# Revit family: Golf-IP40-Plain_Door-syst-NoHosted-CH-en
name_source: partatom
category: Electrical Equipment
units: mm (PartAtom-declared; Revit-internal decimal feet)

## family parameters
Always vertical = Yes
Cut with Voids When Loaded = No
Panel Configuration = Two Columns, Circuits Across
Part Type = Panelboard
Room Calculation Point = No
Round Connector Dimension = Use Diameter
Shared = No
Work Plane-Based = Yes

## types (22) — shared parameters
Default Elevation = 1219 mm
EF000007 - Colour = EV000202 - White
EF000049 - Depth = 98 mm  [stored 0.321522 ft]
EF000116 - RAL-number = 9010
EF000118 - With mounting plate = No
EF000339 - Type of cover = EV004216 - Door
EF001062 - EMC-version = No
EF001088 - Extension possible = Yes
EF001134 - DIN-rail = Yes
EF001596 - Material housing = EV000139 - Plastic
EF004462 - Type of closure = EV000154 - Other
EF005474 - Degree of protection (IP) = EV006415 - IP40
EF006244 - Transparent cover/door = No
EF006306 - With lock = No
EF015776 - Earthing terminal block = No
EF015777 - Neutral terminal block = No
EF015941 - Signal passing door = No
HG000001 - Number of columns = 1
HG000002 - With door or cover = Yes
HG000003 - Range = Golf
HG000005 - Thickness = 3 mm  [stored 0.00984252 ft]
HG000009 - Double swing door = No
HG000010 - Asymmetric doors = No
HG000011 - Empty rows from bottom = No
Manufacturer = Hager
Type Comments = Golf
zero-valued in all types: HG000007 - Number of empty columns, HG000008 - Number of empty rows

## per-type parameters (varying)
| type | EF000003 - Mounting method | EF000008 - Width | EF000040 - Height | EF000218 - Built-in depth | EF000266 - Number of rows | EF000332 - Built-in height | EF000846 - Built-in width | EF001131 - Internal depth | EF002950 - Width in number of modular spacings | EF009212 - Cover model | HG000004 - Manufacturer reference | HG000006 - Flush mounted | Model |
| Recessed mounted IP40 W204 H225 D97.5 4 Modular spacings - VF104PS | EV000128 - Hollow wall | 204 mm | 225 mm  [stored 0.738189 ft] | 72 mm  [stored 0.23622 ft] | 1 | 189 mm  [stored 0.620079 ft] | 170 mm  [stored 0.557743 ft] | 98 mm  [stored 0.321522 ft] | 4 | EV000116 - Closed | VF104PS | Yes | VF104PS |
| Recessed mounted IP40 W275 H225 D97.5 8 Modular spacings - VF108PS | EV000128 - Hollow wall | 275 mm | 225 mm  [stored 0.738189 ft] | 72 mm  [stored 0.23622 ft] | 1 | 189 mm  [stored 0.620079 ft] | 242 mm  [stored 0.793963 ft] | 98 mm  [stored 0.321522 ft] | 8 | EV000116 - Closed | VF108PS | Yes | VF108PS |
| Recessed mounted IP40 W352 H293 D97.5 12 Modular spacings - VF112PS | EV000128 - Hollow wall | 352 mm  [stored 1.15486 ft] | 293 mm | 72 mm  [stored 0.23622 ft] | 1 | 257 mm  [stored 0.843176 ft] | 318 mm  [stored 1.04331 ft] | 98 mm  [stored 0.321522 ft] | 12 | EV000116 - Closed | VF112PS | Yes | VF112PS |
| Recessed mounted IP40 W352 H418 D97.5 12 Modular spacings - VF212PS | EV000128 - Hollow wall | 352 mm  [stored 1.15486 ft] | 418 mm  [stored 1.37139 ft] | 72 mm  [stored 0.23622 ft] | 2 | 382 mm  [stored 1.25328 ft] | 318 mm  [stored 1.04331 ft] | 98 mm  [stored 0.321522 ft] | 12 | EV000116 - Closed | VF212PS | Yes | VF212PS |
| Recessed mounted IP40 W352 H543 D97.5 12 Modular spacings - VF312PS | EV000128 - Hollow wall | 352 mm  [stored 1.15486 ft] | 543 mm  [stored 1.7815 ft] | 72 mm  [stored 0.23622 ft] | 3 | 507 mm  [stored 1.66339 ft] | 318 mm  [stored 1.04331 ft] | 98 mm  [stored 0.321522 ft] | 12 | EV000116 - Closed | VF312PS | Yes | VF312PS |
| Recessed mounted IP40 W352 H688 D97.5 12 Modular spacings - VF412PS | EV000128 - Hollow wall | 352 mm  [stored 1.15486 ft] | 688 mm  [stored 2.25722 ft] | 72 mm  [stored 0.23622 ft] | 4 | 652 mm  [stored 2.13911 ft] | 318 mm  [stored 1.04331 ft] | 98 mm  [stored 0.321522 ft] | 12 | EV000116 - Closed | VF412PS | Yes | VF412PS |
| Recessed mounted IP40 W460 H293 D97.5 18 Modular spacings - VF118PS | EV000128 - Hollow wall | 460 mm  [stored 1.50919 ft] | 293 mm | 72 mm  [stored 0.23622 ft] | 1 | 257 mm  [stored 0.843176 ft] | 426 mm  [stored 1.39764 ft] | 98 mm  [stored 0.321522 ft] | 18 | EV000116 - Closed | VF118PS | Yes | VF118PS |
| Recessed mounted IP40 W460 H418 D97.5 18 Modular spacings - VF218PS | EV000128 - Hollow wall | 460 mm  [stored 1.50919 ft] | 418 mm  [stored 1.37139 ft] | 72 mm  [stored 0.23622 ft] | 2 | 382 mm  [stored 1.25328 ft] | 426 mm  [stored 1.39764 ft] | 98 mm  [stored 0.321522 ft] | 18 | EV000116 - Closed | VF218PS | Yes | VF218PS |
| Recessed mounted IP40 W460 H543 D97.5 18 Modular spacings - VF318PS | EV000128 - Hollow wall | 460 mm  [stored 1.50919 ft] | 543 mm  [stored 1.7815 ft] | 72 mm  [stored 0.23622 ft] | 3 | 507 mm  [stored 1.66339 ft] | 426 mm  [stored 1.39764 ft] | 98 mm  [stored 0.321522 ft] | 18 | EV000116 - Closed | VF318PS | Yes | VF318PS |
| Recessed mounted IP40 W460 H688 D97.5 18 Modular spacings - VF418PS | EV000128 - Hollow wall | 460 mm  [stored 1.50919 ft] | 688 mm  [stored 2.25722 ft] | 72 mm  [stored 0.23622 ft] | 4 | 652 mm  [stored 2.13911 ft] | 426 mm  [stored 1.39764 ft] | 98 mm  [stored 0.321522 ft] | 18 | EV000116 - Closed | VF418PS | Yes | VF418PS |
| Recessed mounted IP40 W532 H293 D97.5 22 Modular spacings - VF122PS | EV000128 - Hollow wall | 532 mm  [stored 1.74541 ft] | 293 mm | 72 mm  [stored 0.23622 ft] | 1 | 257 mm  [stored 0.843176 ft] | 498 mm  [stored 1.63386 ft] | 98 mm  [stored 0.321522 ft] | 22 | EV000116 - Closed | VF122PS | Yes | VF122PS |
| Surface mounted IP40 W137.5 H183.5 D98.5 4 Modular spacings - VS104PS | EV000384 - Surface mounted (plaster) | 138 mm  [stored 0.452756 ft] | 184 mm  [stored 0.603675 ft] | 0 mm  [stored 0 ft] | 1 | 0 mm  [stored 0 ft] | 0 mm  [stored 0 ft] | 98 mm  [stored 0.321522 ft] | 4 | EV000116 - Closed | VS104PS | No | VS104PS |
| Surface mounted IP40 W209.5 H183.5 D98.5 8 Modular spacings - VS108PS | EV000384 - Surface mounted (plaster) | 210 mm  [stored 0.688976 ft] | 184 mm  [stored 0.603675 ft] | 0 mm  [stored 0 ft] | 1 | 0 mm  [stored 0 ft] | 0 mm  [stored 0 ft] | 0 mm  [stored 0 ft] | 8 | 0 | VS108PS | No | VS108PS |
| Surface mounted IP40 W281.5 H251.5 D98.5 12 Modular spacings - VS112PS | EV000384 - Surface mounted (plaster) | 282 mm | 252 mm  [stored 0.826772 ft] | 0 mm  [stored 0 ft] | 1 | 0 mm  [stored 0 ft] | 0 mm  [stored 0 ft] | 98 mm  [stored 0.321522 ft] | 12 | EV000116 - Closed | VS112PS | No | VS112PS |
| Surface mounted IP40 W281.5 H376.5 D98.5 12 Modular spacings - VS212PS | EV000384 - Surface mounted (plaster) | 282 mm | 376 mm  [stored 1.2336 ft] | 0 mm  [stored 0 ft] | 2 | 0 mm  [stored 0 ft] | 0 mm  [stored 0 ft] | 98 mm  [stored 0.321522 ft] | 12 | EV000116 - Closed | VS212PS | No | VS212PS |
| Surface mounted IP40 W281.5 H501.5 D98.5 12 Modular spacings - VS312PS | EV000384 - Surface mounted (plaster) | 282 mm | 502 mm  [stored 1.64698 ft] | 0 mm  [stored 0 ft] | 3 | 0 mm  [stored 0 ft] | 0 mm  [stored 0 ft] | 98 mm  [stored 0.321522 ft] | 12 | EV000116 - Closed | VS312PS | No | VS312PS |
| Surface mounted IP40 W281.5 H646.5 D98.5 12 Modular spacings - VS412PS | EV000384 - Surface mounted (plaster) | 282 mm | 646 mm  [stored 2.11942 ft] | 0 mm  [stored 0 ft] | 4 | 0 mm  [stored 0 ft] | 0 mm  [stored 0 ft] | 98 mm  [stored 0.321522 ft] | 12 | EV000116 - Closed | VS412PS | No | VS412PS |
| Surface mounted IP40 W389.5 H251.5 D98.5 18 Modular spacings - VS118PS | EV000384 - Surface mounted (plaster) | 390 mm  [stored 1.27953 ft] | 252 mm  [stored 0.826772 ft] | 0 mm  [stored 0 ft] | 1 | 0 mm  [stored 0 ft] | 0 mm  [stored 0 ft] | 98 mm  [stored 0.321522 ft] | 18 | EV000116 - Closed | VS118PS | No | VS118PS |
| Surface mounted IP40 W389.5 H376.5 D98.5 18 Modular spacings - VS218PS | EV000384 - Surface mounted (plaster) | 390 mm  [stored 1.27953 ft] | 376 mm  [stored 1.2336 ft] | 0 mm  [stored 0 ft] | 2 | 0 mm  [stored 0 ft] | 0 mm  [stored 0 ft] | 98 mm  [stored 0.321522 ft] | 18 | EV000116 - Closed | VS218PS | No | VS218PS |
| Surface mounted IP40 W389.5 H501.5 D98.5 18 Modular spacings - VS318PS | EV000384 - Surface mounted (plaster) | 390 mm  [stored 1.27953 ft] | 502 mm  [stored 1.64698 ft] | 0 mm  [stored 0 ft] | 3 | 0 mm  [stored 0 ft] | 0 mm  [stored 0 ft] | 98 mm  [stored 0.321522 ft] | 18 | EV000116 - Closed | VS318PS | No | VS318PS |
| Surface mounted IP40 W389.5 H646.5 D98.5 18 Modular spacings - VS418PS | EV000384 - Surface mounted (plaster) | 390 mm  [stored 1.27953 ft] | 646 mm  [stored 2.11942 ft] | 0 mm  [stored 0 ft] | 4 | 0 mm  [stored 0 ft] | 0 mm  [stored 0 ft] | 98 mm  [stored 0.321522 ft] | 18 | EV000116 - Closed | VS418PS | No | VS418PS |
| Surface mounted IP40 W461.5 H251.5 D98.5 22 Modular spacings - VS122PS | EV000384 - Surface mounted (plaster) | 462 mm  [stored 1.51575 ft] | 252 mm  [stored 0.826772 ft] | 0 mm  [stored 0 ft] | 1 | 0 mm  [stored 0 ft] | 0 mm  [stored 0 ft] | 98 mm  [stored 0.321522 ft] | 22 | EV000116 - Closed | VS122PS | No | VS122PS |

note: [stored X ft] marks values corroborated as IEEE doubles in the binary element streams (Revit-internal decimal feet)

## geometry (parser evidence)
native form markers: Sweep x16
no freeform markers — native parametric forms only
